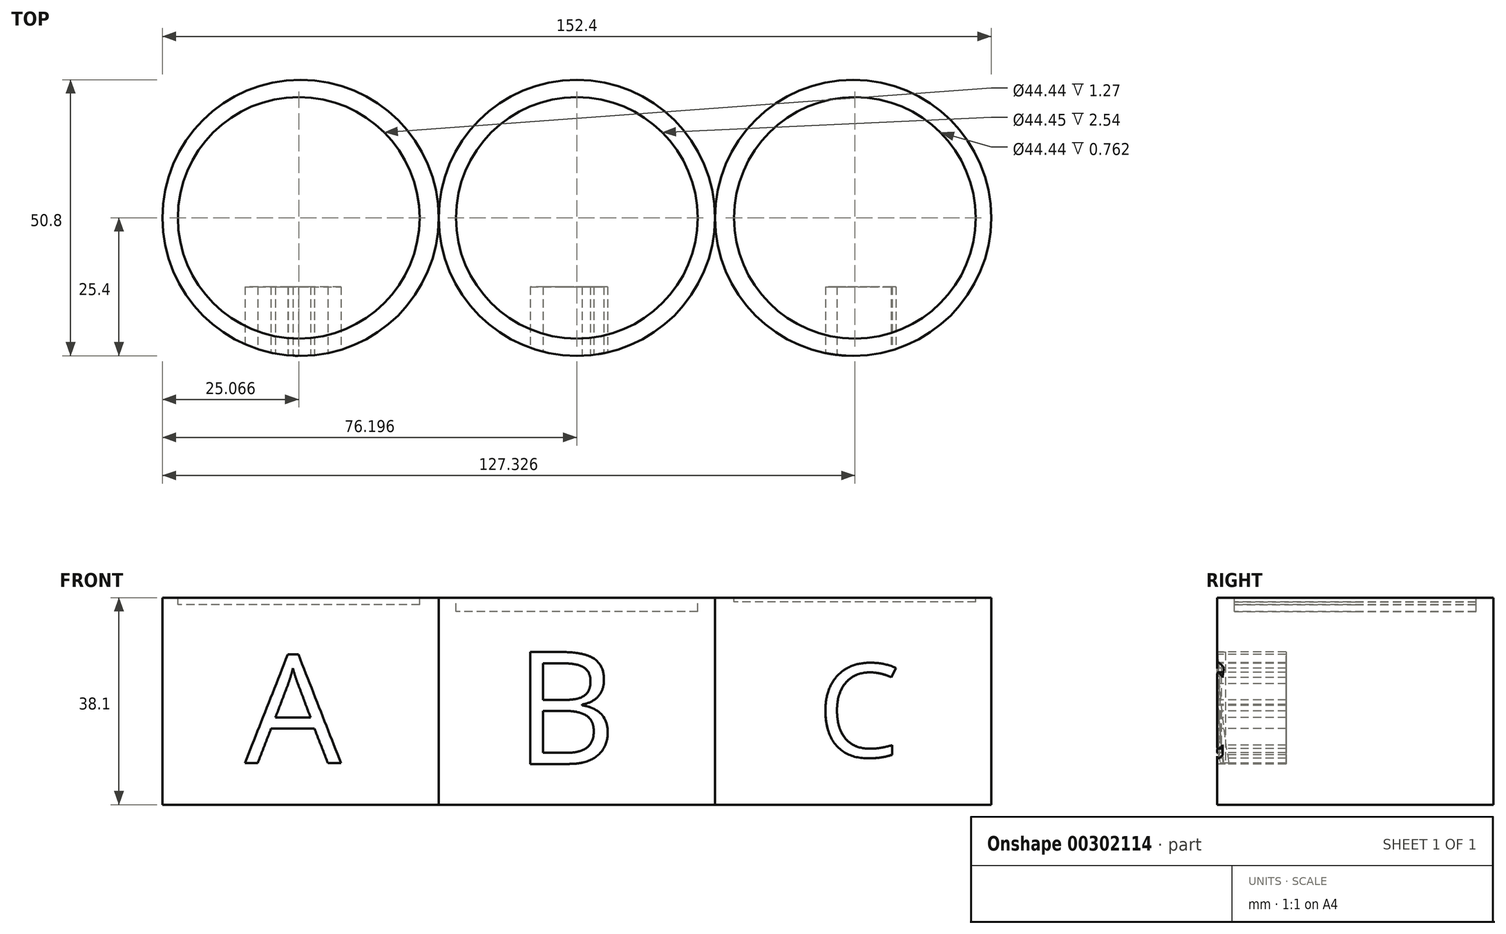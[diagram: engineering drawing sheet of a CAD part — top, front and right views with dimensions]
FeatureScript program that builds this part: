
annotation { "Feature Type Name" : "Feature", "Feature Type Description" : "" }
export const myFeature = defineFeature(function(context is Context, id is Id, definition is map)
    precondition{}
    {
        {
            var Q0;
            Q0=qCreatedBy(makeId("Top.planeOp"),FACE);
            var sketch = newSketch(context, id + "F0", { "sketchPlane" : qUnion([Q0])});
            skCircle(sketch, "E0", {"center": v(-58.35, 0) * mm, "radius": 25.4 * mm});
            skCircle(sketch, "E1", {"center": v(-7.55, 0) * mm, "radius": 25.4 * mm});
            skCircle(sketch, "E2", {"center": v(43.25, 0) * mm, "radius": 25.4 * mm});
            skSolve(sketch);
        }
        {
            var Q0;
            Q0 = qSketchRegion(id + "F0", true);
            extrude(context, id + "F1", {"entities" : qUnion([Q0]), "depth" : 38.1 * mm});
        }
        {
            var Q0;
            Q0=makeQuery(id+"F1.opExtrude","CAP_FACE",FACE,{"disambiguationData":[OSD([sQuery(id+"F0.wireOp",EDGE,"E1")])],"isStart":false});
            var sketch = newSketch(context, id + "F2", { "sketchPlane" : qUnion([Q0])});
            skCircle(sketch, "E3", {"center": v(-58.68, 0) * mm, "radius": 22.22 * mm});
            skCircle(sketch, "E4", {"center": v(-7.55, 0) * mm, "radius": 22.23 * mm});
            skCircle(sketch, "E5", {"center": v(43.58, 0) * mm, "radius": 22.22 * mm});
            skSolve(sketch);
        }
        {
            var Q0;
            Q0=qCreatedBy(makeId("Front.planeOp"),FACE);
            cPlane(context, id + "F3", {"entities" : qUnion([Q0]), "cplaneType" : CPlaneType.OFFSET, "offset" : 25.4 * mm, "width" : 152.4 * mm, "height" : 152.4 * mm});
        }
        {
            var Q0;
            Q0=qCreatedBy(id+"F3.planeOp",FACE);
            var sketch = newSketch(context, id + "F4", { "sketchPlane" : qUnion([Q0])});
            skText(sketch, "E6", { "text": "A", "fontName": "OpenSans-Regular.ttf"});
            skText(sketch, "E7", { "text": "B", "fontName": "OpenSans-Regular.ttf"});
            skText(sketch, "E8", { "text": "C", "fontName": "OpenSans-Regular.ttf"});
            const initialGuessF4  = {"E6": [-0.06858, 0.00764, 1, 0, 0.0201], "E7": [-0.01897, 0.0075, 1, 0, 0.02077], "E8": [0.0367, 0.00877, 1, 0, 0.01726]};
            skSetInitialGuess(sketch, initialGuessF4);
            skSolve(sketch);
        }
        {
            var Q0;
            Q0 = qSketchRegion(id + "F4", true);
            extrude(context, id + "F5", {"entities" : qUnion([Q0]), "operationType" : NewBodyOperationType.REMOVE, "oppositeDirection" : true, "depth" : 12.7 * mm});
        }
        {
            var Q0;
            Q0=makeQuery(id+"F2.imprint","IMPRINT",FACE,{"disambiguationData":[TD([[makeQuery(id+"F2.imprint","IMPRINT",EDGE,{"derivedFrom":sQuery(id+"F2.wireOp",EDGE,"E3")}),1.0]])]});
            extrude(context, id + "F6", {"entities" : qUnion([Q0]), "operationType" : NewBodyOperationType.REMOVE, "oppositeDirection" : true, "depth" : 1.27 * mm});
        }
        {
            var Q0;
            Q0=makeQuery(id+"F2.imprint","IMPRINT",FACE,{"disambiguationData":[TD([[makeQuery(id+"F2.imprint","IMPRINT",EDGE,{"derivedFrom":sQuery(id+"F2.wireOp",EDGE,"E4")}),1.0]])]});
            extrude(context, id + "F7", {"entities" : qUnion([Q0]), "operationType" : NewBodyOperationType.REMOVE, "oppositeDirection" : true, "depth" : 2.54 * mm});
        }
        {
            var Q0;
            Q0=makeQuery(id+"F2.imprint","IMPRINT",FACE,{"disambiguationData":[TD([[makeQuery(id+"F2.imprint","IMPRINT",EDGE,{"derivedFrom":sQuery(id+"F2.wireOp",EDGE,"E5")}),1.0]])]});
            extrude(context, id + "F8", {"entities" : qUnion([Q0]), "operationType" : NewBodyOperationType.REMOVE, "oppositeDirection" : true, "depth" : 0.76 * mm});
        }
    });
